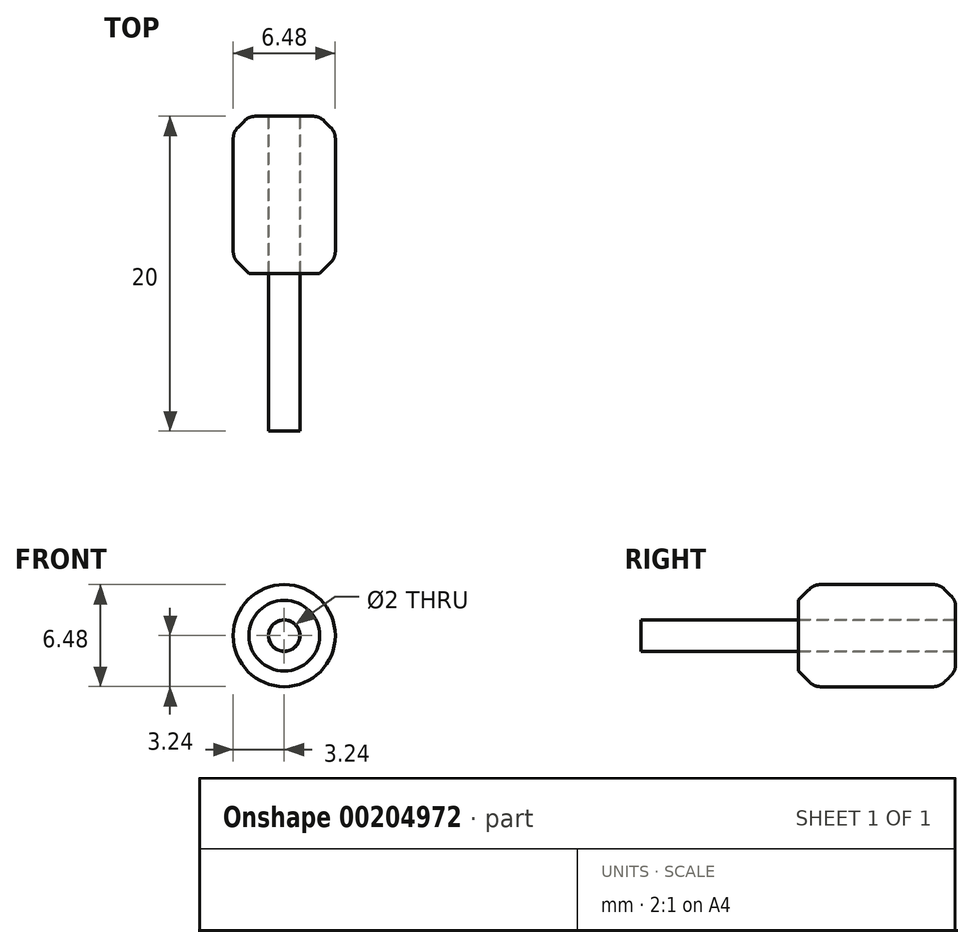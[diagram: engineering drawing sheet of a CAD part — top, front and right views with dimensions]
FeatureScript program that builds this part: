
annotation { "Feature Type Name" : "Feature", "Feature Type Description" : "" }
export const myFeature = defineFeature(function(context is Context, id is Id, definition is map)
    precondition{}
    {
        {
            var Q0;
            Q0=qCreatedBy(makeId("Front.planeOp"),FACE);
            var sketch = newSketch(context, id + "F0", { "sketchPlane" : qUnion([Q0])});
            skCircle(sketch, "E0", {"center": v(0, 0) * mm, "radius": 3.24 * mm});
            skSolve(sketch);
        }
        {
            var Q0;
            Q0=makeQuery(id+"F0.imprint","IMPRINT",FACE,{"disambiguationData":[TD([[makeQuery(id+"F0.imprint","IMPRINT",EDGE,{"derivedFrom":sQuery(id+"F0.wireOp",EDGE,"E0")}),1.0]])]});
            extrude(context, id + "F1", {"entities" : qUnion([Q0]), "depth" : 10 * mm});
        }
        {
            var Q0;
            Q0=makeQuery(id+"F1.opExtrude","SWEPT_FACE",FACE,{"disambiguationData":[OSD([sQuery(id+"F0.wireOp",EDGE,"E0")])]});
            chamfer(context, id + "F2", {"entities" : qUnion([Q0]), "width" : 1 * mm, "tangentPropagation" : true});
        }
        {
            var Q0;
            Q0=qCreatedBy(makeId("Front.planeOp"),FACE);
            var sketch = newSketch(context, id + "F3", { "sketchPlane" : qUnion([Q0])});
            skPoint(sketch, "E1", {"position": v(0, 0) * mm});
            skSolve(sketch);
        }
        {
            var Q0;
            Q0=sQuery(id+"F3.wireOp",VERTEX,"E1");
            var Q1;
            Q1=makeQuery(id+"F1.opExtrude","SWEPT_BODY",BODY,{"disambiguationData":[OSD([sQuery(id+"F0.wireOp",EDGE,"E0")])]});
            hole(context, id + "F4", {"style" : HoleStyle.SIMPLE, "endStyle" : HoleEndStyle.THROUGH, "oppositeDirection" : true, "holeDiameter" : 2 * mm, "locations" : qUnion([Q0]), "scope" : qUnion([Q1]), "isTappedThrough" : true, "startStyle" : HoleStartStyle.SKETCH});
        }
        {
            var Q0;
            {var subQ0=sQuery(id+"F0.wireOp",EDGE,"E0");Q0=makeQuery(id+"F2.opChamfer","BLEND_EDGE",EDGE,{"blendedFrom":[makeQuery(id+"F1.opExtrude","CAP_EDGE",EDGE,{"disambiguationData":[OSD([subQ0])],"isStart":false}),makeQuery(id+"F1.opExtrude","SWEPT_FACE",FACE,{"disambiguationData":[OSD([subQ0])]})],"blendedInto":[makeQuery(id+"F1.opExtrude","SWEPT_FACE",FACE,{"disambiguationData":[OSD([subQ0])]})]});}
            var Q1;
            {var subQ0=sQuery(id+"F0.wireOp",EDGE,"E0");Q1=makeQuery(id+"F2.opChamfer","BLEND_EDGE",EDGE,{"blendedFrom":[makeQuery(id+"F1.opExtrude","CAP_EDGE",EDGE,{"disambiguationData":[OSD([subQ0])],"isStart":true}),makeQuery(id+"F1.opExtrude","SWEPT_FACE",FACE,{"disambiguationData":[OSD([subQ0])]})],"blendedInto":[makeQuery(id+"F1.opExtrude","SWEPT_FACE",FACE,{"disambiguationData":[OSD([subQ0])]})]});}
            var Q2;
            {var subQ0=sQuery(id+"F0.wireOp",EDGE,"E0");Q2=makeQuery(id+"F2.opChamfer","BLEND_FACE",FACE,{"disambiguationData":[OSD([subQ0]),TDD([makeQuery(id+"F1.opExtrude","CAP_EDGE",EDGE,{"disambiguationData":[OSD([subQ0])],"isStart":true})])]});}
            var Q3;
            Q3=makeQuery(id+"F4.hole-0.boolean.opBoolean","INTERSECT",EDGE,{"derivedFrom":[makeQuery(id+"F1.opExtrude","CAP_FACE",FACE,{"disambiguationData":[OSD([sQuery(id+"F0.wireOp",EDGE,"E0")])],"isStart":false}),makeQuery(id+"F4.hole-0.opRevolve","SWEPT_FACE",FACE,{"disambiguationData":[OSD([sQuery(id+"F4.hole-0.sketch.wireOp",EDGE,"core_line_2")])]})]});
            fillet(context, id + "F5", {"entities" : qUnion([Q0, Q1, Q2, Q3]), "radius" : 1 * mm, "tangentPropagation" : true, "allowEdgeOverflow" : false});
        }
        {
            var Q0;
            Q0=qCreatedBy(makeId("Front.planeOp"),FACE);
            var sketch = newSketch(context, id + "F6", { "sketchPlane" : qUnion([Q0])});
            skCircle(sketch, "E2", {"center": v(0, 0) * mm, "radius": 0.99 * mm});
            skSolve(sketch);
        }
        {
            var Q0;
            Q0 = qSketchRegion(id + "F6", true);
            extrude(context, id + "F7", {"entities" : qUnion([Q0]), "depth" : 20 * mm});
        }
    });
